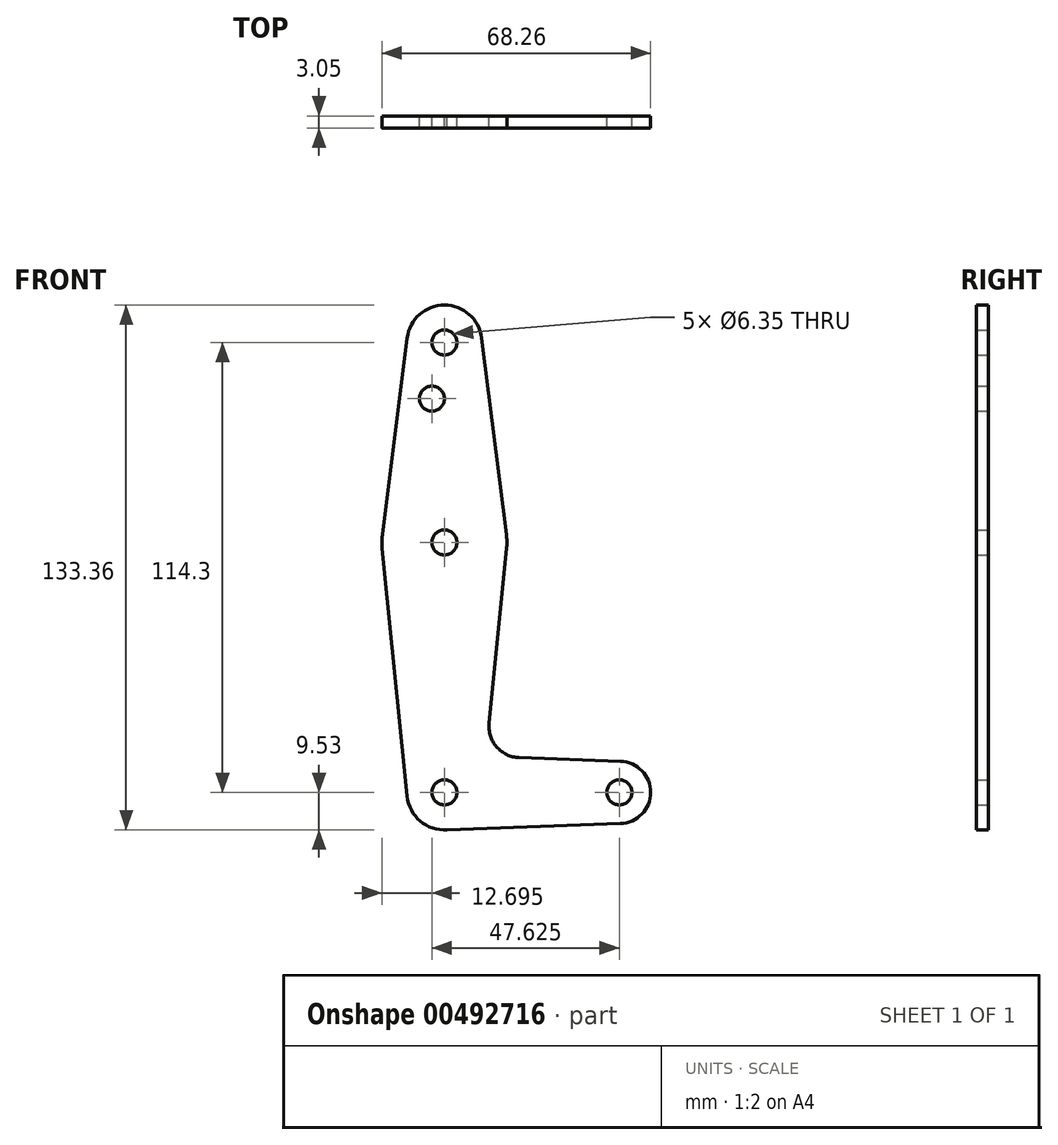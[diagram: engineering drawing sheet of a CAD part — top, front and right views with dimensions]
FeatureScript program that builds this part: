
annotation { "Feature Type Name" : "Feature", "Feature Type Description" : "" }
export const myFeature = defineFeature(function(context is Context, id is Id, definition is map)
    precondition{}
    {
        {
            var Q0;
            Q0=qCreatedBy(makeId("Front.planeOp"),FACE);
            var sketch = newSketch(context, id + "F0", { "sketchPlane" : qUnion([Q0])});
            skLineSegment(sketch, "E0", {"start": v(0, 0) * mm, "end": v(0, 114.3) * mm});
            skLineSegment(sketch, "E1", {"start": v(0, 0) * mm, "end": v(44.45, 0) * mm});
            skCircle(sketch, "E2", {"center": v(0, 114.3) * mm, "radius": 9.53 * mm});
            skCircle(sketch, "E3", {"center": v(0, 0) * mm, "radius": 9.53 * mm});
            skCircle(sketch, "E4", {"center": v(44.45, 0) * mm, "radius": 7.94 * mm});
            skCircle(sketch, "E5", {"center": v(0, 63.5) * mm, "radius": 15.88 * mm});
            skLineSegment(sketch, "E6", {"start": v(-9.45, 115.5) * mm, "end": v(-15.75, 65.48) * mm});
            skLineSegment(sketch, "E7", {"start": v(9.45, 115.5) * mm, "end": v(15.75, 65.48) * mm});
            skLineSegment(sketch, "E8", {"start": v(18.97, 8.85) * mm, "end": v(44.73, 7.93) * mm});
            skLineSegment(sketch, "E9", {"start": v(0, -9.53) * mm, "end": v(44.73, -7.93) * mm});
            skLineSegment(sketch, "E10", {"start": v(15.8, 61.91) * mm, "end": v(11.34, 17.59) * mm});
            skLineSegment(sketch, "E11", {"start": v(-15.8, 61.91) * mm, "end": v(-9.48, -0.95) * mm});
            skCircle(sketch, "E12", {"center": v(0, 114.3) * mm, "radius": 3.18 * mm});
            skCircle(sketch, "E13", {"center": v(0, 63.5) * mm, "radius": 3.18 * mm});
            skCircle(sketch, "E14", {"center": v(0, 0) * mm, "radius": 3.18 * mm});
            skCircle(sketch, "E15", {"center": v(44.45, 0) * mm, "radius": 3.18 * mm});
            skCircle(sketch, "E16", {"center": v(-3.18, 100.03) * mm, "radius": 3.18 * mm});
            skArc(sketch, "E17.filletArc", {"start": v(11.34, 17.59) * mm, "mid": v(13.26, 11.57) * mm, "end": v(18.97, 8.85) * mm});
            skSolve(sketch);
        }
        {
            var Q0;
            Q0 = qSketchRegion(id + "F0", true);
            var Q1;
            {var subQ0=sQuery(id+"F0.wireOp",EDGE,"E14");var subQ1=sQuery(id+"F0.wireOp",EDGE,"E0");var subQ2=makeQuery(id+"F0.imprint","INTERSECT",VERTEX,{"derivedFrom":[subQ1,subQ0]});Q1=makeQuery(id+"F0.imprint","IMPRINT",FACE,{"disambiguationData":[TD([[makeQuery(id+"F0.imprint","IMPRINT",EDGE,{"disambiguationData":[TD([[subQ2,-1.0]])],"derivedFrom":subQ1}),-1.0]])]});}
            extrude(context, id + "F1", {"entities" : qUnion([Q0, Q1]), "depth" : 3.05 * mm});
        }
    });
